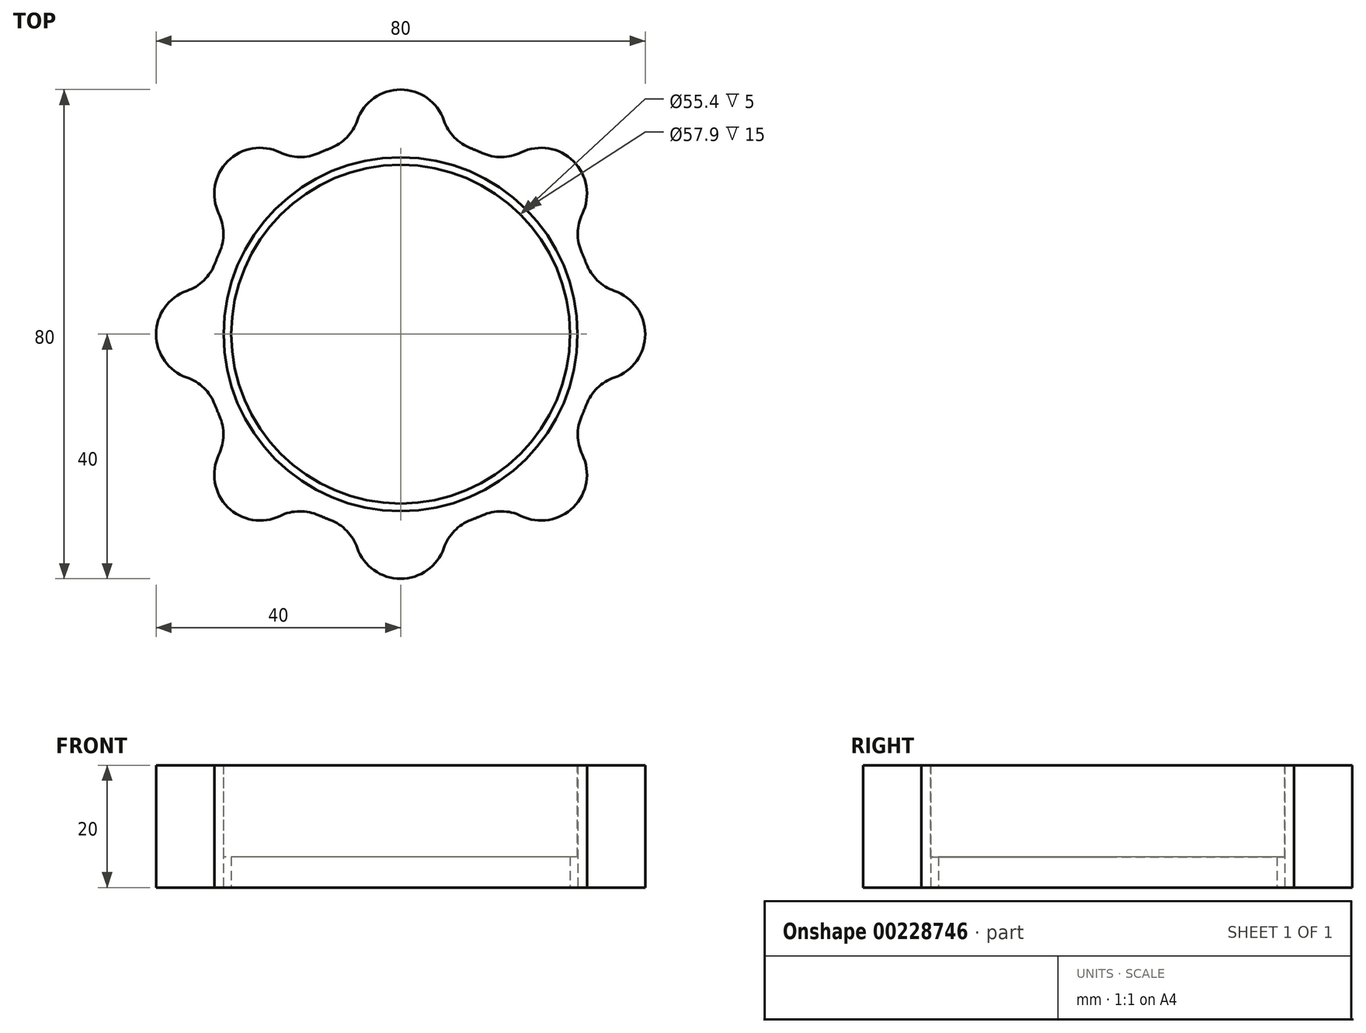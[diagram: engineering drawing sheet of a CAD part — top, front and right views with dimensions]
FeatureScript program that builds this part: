
annotation { "Feature Type Name" : "Feature", "Feature Type Description" : "" }
export const myFeature = defineFeature(function(context is Context, id is Id, definition is map)
    precondition{}
    {
        {
            var Q0;
            Q0=qCreatedBy(makeId("Top.planeOp"),FACE);
            var sketch = newSketch(context, id + "F0", { "sketchPlane" : qUnion([Q0])});
            skCircle(sketch, "E0", {"center": v(0, 0) * mm, "radius": 27.7 * mm});
            skCircle(sketch, "E1", {"center": v(0, 0) * mm, "radius": 40 * mm, "construction": true});
            skArc(sketch, "E2", {"start": v(-11.52, 30.4) * mm, "mid": v(-12.44, 30.03) * mm, "end": v(-13.35, 29.63) * mm});
            skArc(sketch, "E3", {"start": v(7.09, 34.95) * mm, "mid": v(0, 40) * mm, "end": v(-7.09, 34.95) * mm});
            skPoint(sketch, "E4.visualSharp", {"position": v(-7.45, 31.63) * mm});
            skArc(sketch, "E4.filletArc", {"start": v(-11.52, 30.4) * mm, "mid": v(-8.8, 32.18) * mm, "end": v(-7.09, 34.95) * mm});
            skPoint(sketch, "E5.visualSharp", {"position": v(7.45, 31.63) * mm});
            skArc(sketch, "E5.filletArc", {"start": v(7.09, 34.95) * mm, "mid": v(8.8, 32.18) * mm, "end": v(11.52, 30.4) * mm});
            skArc(sketch, "E6.1.0", {"start": v(-29.63, 13.35) * mm, "mid": v(-28.97, 16.53) * mm, "end": v(-29.73, 19.7) * mm});
            skArc(sketch, "E6.1.1", {"start": v(-19.7, 29.73) * mm, "mid": v(-28.28, 28.28) * mm, "end": v(-29.73, 19.7) * mm});
            skArc(sketch, "E6.1.2", {"start": v(-19.7, 29.73) * mm, "mid": v(-16.53, 28.97) * mm, "end": v(-13.35, 29.63) * mm});
            skArc(sketch, "E6.2.0", {"start": v(-30.4, -11.52) * mm, "mid": v(-32.18, -8.8) * mm, "end": v(-34.95, -7.09) * mm});
            skArc(sketch, "E6.2.1", {"start": v(-34.95, 7.09) * mm, "mid": v(-40, 0) * mm, "end": v(-34.95, -7.09) * mm});
            skArc(sketch, "E6.2.2", {"start": v(-34.95, 7.09) * mm, "mid": v(-32.18, 8.8) * mm, "end": v(-30.4, 11.52) * mm});
            skArc(sketch, "E6.3.0", {"start": v(-13.35, -29.63) * mm, "mid": v(-16.53, -28.97) * mm, "end": v(-19.7, -29.73) * mm});
            skArc(sketch, "E6.3.1", {"start": v(-29.73, -19.7) * mm, "mid": v(-28.28, -28.28) * mm, "end": v(-19.7, -29.73) * mm});
            skArc(sketch, "E6.3.2", {"start": v(-29.73, -19.7) * mm, "mid": v(-28.97, -16.53) * mm, "end": v(-29.63, -13.35) * mm});
            skArc(sketch, "E6.4.0", {"start": v(11.52, -30.4) * mm, "mid": v(8.8, -32.18) * mm, "end": v(7.09, -34.95) * mm});
            skArc(sketch, "E6.4.1", {"start": v(-7.09, -34.95) * mm, "mid": v(0, -40) * mm, "end": v(7.09, -34.95) * mm});
            skArc(sketch, "E6.4.2", {"start": v(-7.09, -34.95) * mm, "mid": v(-8.8, -32.18) * mm, "end": v(-11.52, -30.4) * mm});
            skArc(sketch, "E6.5.0", {"start": v(29.63, -13.35) * mm, "mid": v(28.97, -16.53) * mm, "end": v(29.73, -19.7) * mm});
            skArc(sketch, "E6.5.1", {"start": v(19.7, -29.73) * mm, "mid": v(28.28, -28.28) * mm, "end": v(29.73, -19.7) * mm});
            skArc(sketch, "E6.5.2", {"start": v(19.7, -29.73) * mm, "mid": v(16.53, -28.97) * mm, "end": v(13.35, -29.63) * mm});
            skArc(sketch, "E6.6.0", {"start": v(30.4, 11.52) * mm, "mid": v(32.18, 8.8) * mm, "end": v(34.95, 7.09) * mm});
            skArc(sketch, "E6.6.1", {"start": v(34.95, -7.09) * mm, "mid": v(40, 0) * mm, "end": v(34.95, 7.09) * mm});
            skArc(sketch, "E6.6.2", {"start": v(34.95, -7.09) * mm, "mid": v(32.18, -8.8) * mm, "end": v(30.4, -11.52) * mm});
            skArc(sketch, "E6.7.0", {"start": v(13.35, 29.63) * mm, "mid": v(16.53, 28.97) * mm, "end": v(19.7, 29.73) * mm});
            skArc(sketch, "E6.7.1", {"start": v(29.73, 19.7) * mm, "mid": v(28.28, 28.28) * mm, "end": v(19.7, 29.73) * mm});
            skArc(sketch, "E6.7.2", {"start": v(29.73, 19.7) * mm, "mid": v(28.97, 16.53) * mm, "end": v(29.63, 13.35) * mm});
            skArc(sketch, "E7.trimOffspring", {"start": v(-29.63, 13.35) * mm, "mid": v(-30.03, 12.44) * mm, "end": v(-30.4, 11.52) * mm});
            skArc(sketch, "E8.trimOffspring", {"start": v(-30.4, -11.52) * mm, "mid": v(-30.03, -12.44) * mm, "end": v(-29.63, -13.35) * mm});
            skArc(sketch, "E9.trimOffspring", {"start": v(-13.35, -29.63) * mm, "mid": v(-12.44, -30.03) * mm, "end": v(-11.52, -30.4) * mm});
            skArc(sketch, "E10.trimOffspring", {"start": v(11.52, -30.4) * mm, "mid": v(12.44, -30.03) * mm, "end": v(13.35, -29.63) * mm});
            skArc(sketch, "E11.trimOffspring", {"start": v(29.63, -13.35) * mm, "mid": v(30.03, -12.44) * mm, "end": v(30.4, -11.52) * mm});
            skArc(sketch, "E12.trimOffspring", {"start": v(30.4, 11.52) * mm, "mid": v(30.03, 12.44) * mm, "end": v(29.63, 13.35) * mm});
            skArc(sketch, "E13.trimOffspring", {"start": v(13.35, 29.63) * mm, "mid": v(12.44, 30.03) * mm, "end": v(11.52, 30.4) * mm});
            skSolve(sketch);
        }
        {
            var Q0;
            Q0 = qSketchRegion(id + "F0", true);
            extrude(context, id + "F1", {"entities" : qUnion([Q0]), "depth" : 20 * mm});
        }
        {
            var Q0;
            Q0=makeQuery(id+"F1.opExtrude","CAP_FACE",FACE,{"disambiguationData":[OSD([sQuery(id+"F0.wireOp",EDGE,"E0"),sQuery(id+"F0.wireOp",EDGE,"E2"),sQuery(id+"F0.wireOp",EDGE,"E3"),sQuery(id+"F0.wireOp",EDGE,"E4.filletArc"),sQuery(id+"F0.wireOp",EDGE,"E5.filletArc"),sQuery(id+"F0.wireOp",EDGE,"E6.1.0"),sQuery(id+"F0.wireOp",EDGE,"E6.1.1"),sQuery(id+"F0.wireOp",EDGE,"E6.1.2"),sQuery(id+"F0.wireOp",EDGE,"E6.2.0"),sQuery(id+"F0.wireOp",EDGE,"E6.2.1"),sQuery(id+"F0.wireOp",EDGE,"E6.2.2"),sQuery(id+"F0.wireOp",EDGE,"E6.3.0"),sQuery(id+"F0.wireOp",EDGE,"E6.3.1"),sQuery(id+"F0.wireOp",EDGE,"E6.3.2"),sQuery(id+"F0.wireOp",EDGE,"E6.4.0"),sQuery(id+"F0.wireOp",EDGE,"E6.4.1"),sQuery(id+"F0.wireOp",EDGE,"E6.4.2"),sQuery(id+"F0.wireOp",EDGE,"E6.5.0"),sQuery(id+"F0.wireOp",EDGE,"E6.5.1"),sQuery(id+"F0.wireOp",EDGE,"E6.5.2"),sQuery(id+"F0.wireOp",EDGE,"E6.6.0"),sQuery(id+"F0.wireOp",EDGE,"E6.6.1"),sQuery(id+"F0.wireOp",EDGE,"E6.6.2"),sQuery(id+"F0.wireOp",EDGE,"E6.7.0"),sQuery(id+"F0.wireOp",EDGE,"E6.7.1"),sQuery(id+"F0.wireOp",EDGE,"E6.7.2"),sQuery(id+"F0.wireOp",EDGE,"E7.trimOffspring"),sQuery(id+"F0.wireOp",EDGE,"E8.trimOffspring"),sQuery(id+"F0.wireOp",EDGE,"E9.trimOffspring"),sQuery(id+"F0.wireOp",EDGE,"E10.trimOffspring"),sQuery(id+"F0.wireOp",EDGE,"E11.trimOffspring"),sQuery(id+"F0.wireOp",EDGE,"E12.trimOffspring"),sQuery(id+"F0.wireOp",EDGE,"E13.trimOffspring")])],"isStart":false});
            var sketch = newSketch(context, id + "F2", { "sketchPlane" : qUnion([Q0])});
            skCircle(sketch, "E14", {"center": v(0, 0) * mm, "radius": 28.95 * mm});
            skSolve(sketch);
        }
        {
            var Q0;
            Q0 = qSketchRegion(id + "F2", true);
            extrude(context, id + "F3", {"entities" : qUnion([Q0]), "operationType" : NewBodyOperationType.REMOVE, "oppositeDirection" : true, "depth" : 15 * mm});
        }
    });
